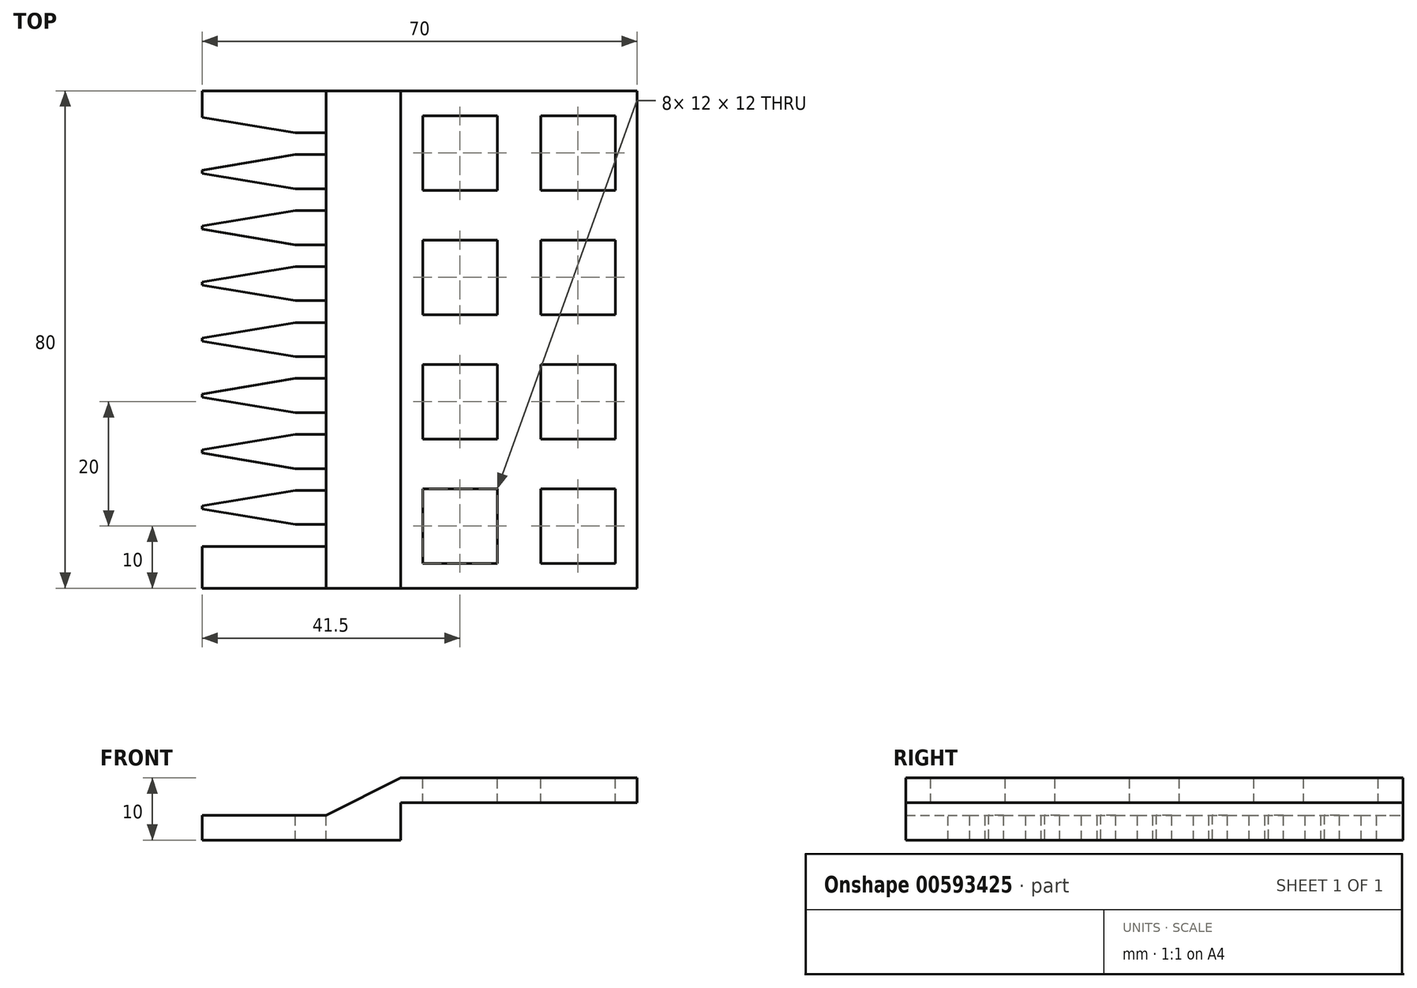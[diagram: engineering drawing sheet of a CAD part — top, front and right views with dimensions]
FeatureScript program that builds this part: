
annotation { "Feature Type Name" : "Feature", "Feature Type Description" : "" }
export const myFeature = defineFeature(function(context is Context, id is Id, definition is map)
    precondition{}
    {
        {
            var Q0;
            Q0=qCreatedBy(makeId("Front.planeOp"),FACE);
            var sketch = newSketch(context, id + "F0", { "sketchPlane" : qUnion([Q0])});
            skLineSegment(sketch, "E0", {"start": v(0, 0) * mm, "end": v(0, 4) * mm});
            skLineSegment(sketch, "E1", {"start": v(0, 4) * mm, "end": v(20, 4) * mm});
            skLineSegment(sketch, "E2", {"start": v(20, 4) * mm, "end": v(20, 10) * mm});
            skLineSegment(sketch, "E3", {"start": v(20, 10) * mm, "end": v(100, 10) * mm});
            skLineSegment(sketch, "E4", {"start": v(100, 10) * mm, "end": v(100, 6) * mm});
            skLineSegment(sketch, "E5", {"start": v(100, 6) * mm, "end": v(32, 6) * mm});
            skLineSegment(sketch, "E6", {"start": v(32, 6) * mm, "end": v(32, 0) * mm});
            skLineSegment(sketch, "E7", {"start": v(32, 0) * mm, "end": v(0, 0) * mm});
            skSolve(sketch);
        }
        {
            var Q0;
            Q0 = qSketchRegion(id + "F0", true);
            extrude(context, id + "F1", {"entities" : qUnion([Q0]), "depth" : 80 * mm, "offsetDistance" : 25 * mm});
        }
        {
            var Q0;
            Q0=makeQuery(id+"F1.opExtrude","SWEPT_FACE",FACE,{"disambiguationData":[OSD([sQuery(id+"F0.wireOp",EDGE,"E1")])]});
            var sketch = newSketch(context, id + "F2", { "sketchPlane" : qUnion([Q0])});
            skLineSegment(sketch, "E8", {"start": v(0, -40) * mm, "end": v(20, -40) * mm, "construction": true});
            skLineSegment(sketch, "E9.bottom", {"start": v(0, -37.25) * mm, "end": v(20, -37.25) * mm});
            skLineSegment(sketch, "E9.top", {"start": v(0, -33.75) * mm, "end": v(20, -33.75) * mm});
            skLineSegment(sketch, "E9.left", {"start": v(0, -37.25) * mm, "end": v(0, -33.75) * mm});
            skLineSegment(sketch, "E9.right", {"start": v(20, -37.25) * mm, "end": v(20, -33.75) * mm});
            skLineSegment(sketch, "E10.bottom", {"start": v(0, -28.25) * mm, "end": v(20, -28.25) * mm});
            skLineSegment(sketch, "E10.top", {"start": v(0, -24.75) * mm, "end": v(20, -24.75) * mm});
            skLineSegment(sketch, "E10.left", {"start": v(0, -28.25) * mm, "end": v(0, -24.75) * mm});
            skLineSegment(sketch, "E10.right", {"start": v(20, -28.25) * mm, "end": v(20, -24.75) * mm});
            skLineSegment(sketch, "E11.bottom", {"start": v(0, -19.25) * mm, "end": v(20, -19.25) * mm});
            skLineSegment(sketch, "E11.top", {"start": v(0, -15.75) * mm, "end": v(20, -15.75) * mm});
            skLineSegment(sketch, "E11.left", {"start": v(0, -19.25) * mm, "end": v(0, -15.75) * mm});
            skLineSegment(sketch, "E11.right", {"start": v(20, -19.25) * mm, "end": v(20, -15.75) * mm});
            skLineSegment(sketch, "E12.bottom", {"start": v(0, -10.25) * mm, "end": v(20, -10.25) * mm});
            skLineSegment(sketch, "E12.top", {"start": v(0, -6.75) * mm, "end": v(20, -6.75) * mm});
            skLineSegment(sketch, "E12.left", {"start": v(0, -10.25) * mm, "end": v(0, -6.75) * mm});
            skLineSegment(sketch, "E12.right", {"start": v(20, -10.25) * mm, "end": v(20, -6.75) * mm});
            skLineSegment(sketch, "E13", {"start": v(10, -10.25) * mm, "end": v(10, -15.75) * mm, "construction": true});
            skLineSegment(sketch, "E14", {"start": v(10, -24.75) * mm, "end": v(10, -19.25) * mm, "construction": true});
            skLineSegment(sketch, "E15", {"start": v(10, -28.25) * mm, "end": v(10, -33.75) * mm, "construction": true});
            skLineSegment(sketch, "E16.MirrorCS", {"start": v(20, -69.75) * mm, "end": v(20, -73.25) * mm});
            skLineSegment(sketch, "E17.MirrorCS", {"start": v(0, -55.25) * mm, "end": v(20, -55.25) * mm});
            skLineSegment(sketch, "E18.MirrorCS", {"start": v(0, -46.25) * mm, "end": v(20, -46.25) * mm});
            skLineSegment(sketch, "E19.MirrorCS", {"start": v(0, -60.75) * mm, "end": v(20, -60.75) * mm});
            skLineSegment(sketch, "E20.MirrorCS", {"start": v(10, -69.75) * mm, "end": v(10, -64.25) * mm, "construction": true});
            skLineSegment(sketch, "E21.MirrorCS", {"start": v(0, -42.75) * mm, "end": v(0, -46.25) * mm});
            skLineSegment(sketch, "E22.MirrorCS", {"start": v(0, -73.25) * mm, "end": v(20, -73.25) * mm});
            skLineSegment(sketch, "E23.MirrorCS", {"start": v(0, -51.75) * mm, "end": v(0, -55.25) * mm});
            skLineSegment(sketch, "E24.MirrorCS", {"start": v(0, -42.75) * mm, "end": v(20, -42.75) * mm});
            skLineSegment(sketch, "E25.MirrorCS", {"start": v(10, -55.25) * mm, "end": v(10, -60.75) * mm, "construction": true});
            skLineSegment(sketch, "E26.MirrorCS", {"start": v(0, -69.75) * mm, "end": v(0, -73.25) * mm});
            skLineSegment(sketch, "E27.MirrorCS", {"start": v(20, -51.75) * mm, "end": v(20, -55.25) * mm});
            skLineSegment(sketch, "E28.MirrorCS", {"start": v(20, -42.75) * mm, "end": v(20, -46.25) * mm});
            skLineSegment(sketch, "E29.MirrorCS", {"start": v(0, -60.75) * mm, "end": v(0, -64.25) * mm});
            skLineSegment(sketch, "E30.MirrorCS", {"start": v(0, -69.75) * mm, "end": v(20, -69.75) * mm});
            skLineSegment(sketch, "E31.MirrorCS", {"start": v(10, -51.75) * mm, "end": v(10, -46.25) * mm, "construction": true});
            skLineSegment(sketch, "E32.MirrorCS", {"start": v(20, -60.75) * mm, "end": v(20, -64.25) * mm});
            skLineSegment(sketch, "E33.MirrorCS", {"start": v(0, -51.75) * mm, "end": v(20, -51.75) * mm});
            skLineSegment(sketch, "E34.MirrorCS", {"start": v(0, -64.25) * mm, "end": v(20, -64.25) * mm});
            skSolve(sketch);
        }
        {
            var Q0;
            Q0 = qSketchRegion(id + "F2", true);
            extrude(context, id + "F3", {"entities" : qUnion([Q0]), "operationType" : NewBodyOperationType.REMOVE, "endBound" : BoundingType.THROUGH_ALL, "oppositeDirection" : true, "depth" : 25 * mm, "offsetDistance" : 25 * mm});
        }
        {
            var Q0;
            Q0=makeQuery(id+"F1.opExtrude","SWEPT_EDGE",EDGE,{"disambiguationData":[OSD([sQuery(id+"F0.wireOp",EDGE,"E2"),sQuery(id+"F0.wireOp",EDGE,"E3")])]});
            chamfer(context, id + "F4", {"entities" : qUnion([Q0]), "chamferType" : ChamferType.TWO_OFFSETS, "width1" : 6 * mm, "oppositeDirection" : false, "width2" : 12 * mm, "tangentPropagation" : true});
        }
        {
            var Q0;
            Q0=makeQuery(id+"F3.boolean.opBoolean","COPY",EDGE,{"derivedFrom":makeQuery(id+"F3.opExtrude","SWEPT_EDGE",EDGE,{"disambiguationData":[OSD([sQuery(id+"F0.wireOp",EDGE,"E0"),sQuery(id+"F0.wireOp",EDGE,"E1"),sQuery(id+"F2.wireOp",EDGE,"E12.top"),sQuery(id+"F2.wireOp",EDGE,"E12.left")])]})});
            var Q1;
            Q1=makeQuery(id+"F3.boolean.opBoolean","COPY",EDGE,{"derivedFrom":makeQuery(id+"F3.opExtrude","SWEPT_EDGE",EDGE,{"disambiguationData":[OSD([sQuery(id+"F0.wireOp",EDGE,"E0"),sQuery(id+"F0.wireOp",EDGE,"E1"),sQuery(id+"F2.wireOp",EDGE,"E11.top"),sQuery(id+"F2.wireOp",EDGE,"E11.left")])]})});
            var Q2;
            Q2=makeQuery(id+"F3.boolean.opBoolean","COPY",EDGE,{"derivedFrom":makeQuery(id+"F3.opExtrude","SWEPT_EDGE",EDGE,{"disambiguationData":[OSD([sQuery(id+"F0.wireOp",EDGE,"E0"),sQuery(id+"F0.wireOp",EDGE,"E1"),sQuery(id+"F2.wireOp",EDGE,"E10.top"),sQuery(id+"F2.wireOp",EDGE,"E10.left")])]})});
            var Q3;
            Q3=makeQuery(id+"F3.boolean.opBoolean","COPY",EDGE,{"derivedFrom":makeQuery(id+"F3.opExtrude","SWEPT_EDGE",EDGE,{"disambiguationData":[OSD([sQuery(id+"F0.wireOp",EDGE,"E0"),sQuery(id+"F0.wireOp",EDGE,"E1"),sQuery(id+"F2.wireOp",EDGE,"E9.top"),sQuery(id+"F2.wireOp",EDGE,"E9.left")])]})});
            var Q4;
            Q4=makeQuery(id+"F3.boolean.opBoolean","COPY",EDGE,{"derivedFrom":makeQuery(id+"F3.opExtrude","SWEPT_EDGE",EDGE,{"disambiguationData":[OSD([sQuery(id+"F0.wireOp",EDGE,"E0"),sQuery(id+"F0.wireOp",EDGE,"E1"),sQuery(id+"F2.wireOp",EDGE,"E21.MirrorCS"),sQuery(id+"F2.wireOp",EDGE,"E24.MirrorCS")])]})});
            var Q5;
            Q5=makeQuery(id+"F3.boolean.opBoolean","COPY",EDGE,{"derivedFrom":makeQuery(id+"F3.opExtrude","SWEPT_EDGE",EDGE,{"disambiguationData":[OSD([sQuery(id+"F0.wireOp",EDGE,"E0"),sQuery(id+"F0.wireOp",EDGE,"E1"),sQuery(id+"F2.wireOp",EDGE,"E23.MirrorCS"),sQuery(id+"F2.wireOp",EDGE,"E33.MirrorCS")])]})});
            var Q6;
            Q6=makeQuery(id+"F3.boolean.opBoolean","COPY",EDGE,{"derivedFrom":makeQuery(id+"F3.opExtrude","SWEPT_EDGE",EDGE,{"disambiguationData":[OSD([sQuery(id+"F0.wireOp",EDGE,"E0"),sQuery(id+"F0.wireOp",EDGE,"E1"),sQuery(id+"F2.wireOp",EDGE,"E19.MirrorCS"),sQuery(id+"F2.wireOp",EDGE,"E29.MirrorCS")])]})});
            var Q7;
            Q7=makeQuery(id+"F3.boolean.opBoolean","COPY",EDGE,{"derivedFrom":makeQuery(id+"F3.opExtrude","SWEPT_EDGE",EDGE,{"disambiguationData":[OSD([sQuery(id+"F0.wireOp",EDGE,"E0"),sQuery(id+"F0.wireOp",EDGE,"E1"),sQuery(id+"F2.wireOp",EDGE,"E26.MirrorCS"),sQuery(id+"F2.wireOp",EDGE,"E30.MirrorCS")])]})});
            chamfer(context, id + "F5", {"entities" : qUnion([Q0, Q1, Q2, Q3, Q4, Q5, Q6, Q7]), "chamferType" : ChamferType.TWO_OFFSETS, "width1" : 2.5 * mm, "oppositeDirection" : false, "width2" : 15 * mm, "tangentPropagation" : true});
        }
        {
            var Q0;
            Q0=makeQuery(id+"F3.boolean.opBoolean","COPY",EDGE,{"derivedFrom":makeQuery(id+"F3.opExtrude","SWEPT_EDGE",EDGE,{"disambiguationData":[OSD([sQuery(id+"F0.wireOp",EDGE,"E0"),sQuery(id+"F0.wireOp",EDGE,"E1"),sQuery(id+"F2.wireOp",EDGE,"E12.bottom"),sQuery(id+"F2.wireOp",EDGE,"E12.left")])]})});
            var Q1;
            Q1=makeQuery(id+"F3.boolean.opBoolean","COPY",EDGE,{"derivedFrom":makeQuery(id+"F3.opExtrude","SWEPT_EDGE",EDGE,{"disambiguationData":[OSD([sQuery(id+"F0.wireOp",EDGE,"E0"),sQuery(id+"F0.wireOp",EDGE,"E1"),sQuery(id+"F2.wireOp",EDGE,"E11.bottom"),sQuery(id+"F2.wireOp",EDGE,"E11.left")])]})});
            var Q2;
            Q2=makeQuery(id+"F3.boolean.opBoolean","COPY",EDGE,{"derivedFrom":makeQuery(id+"F3.opExtrude","SWEPT_EDGE",EDGE,{"disambiguationData":[OSD([sQuery(id+"F0.wireOp",EDGE,"E0"),sQuery(id+"F0.wireOp",EDGE,"E1"),sQuery(id+"F2.wireOp",EDGE,"E10.bottom"),sQuery(id+"F2.wireOp",EDGE,"E10.left")])]})});
            var Q3;
            Q3=makeQuery(id+"F3.boolean.opBoolean","COPY",EDGE,{"derivedFrom":makeQuery(id+"F3.opExtrude","SWEPT_EDGE",EDGE,{"disambiguationData":[OSD([sQuery(id+"F0.wireOp",EDGE,"E0"),sQuery(id+"F0.wireOp",EDGE,"E1"),sQuery(id+"F2.wireOp",EDGE,"E9.bottom"),sQuery(id+"F2.wireOp",EDGE,"E9.left")])]})});
            var Q4;
            Q4=makeQuery(id+"F3.boolean.opBoolean","COPY",EDGE,{"derivedFrom":makeQuery(id+"F3.opExtrude","SWEPT_EDGE",EDGE,{"disambiguationData":[OSD([sQuery(id+"F0.wireOp",EDGE,"E0"),sQuery(id+"F0.wireOp",EDGE,"E1"),sQuery(id+"F2.wireOp",EDGE,"E18.MirrorCS"),sQuery(id+"F2.wireOp",EDGE,"E21.MirrorCS")])]})});
            var Q5;
            Q5=makeQuery(id+"F3.boolean.opBoolean","COPY",EDGE,{"derivedFrom":makeQuery(id+"F3.opExtrude","SWEPT_EDGE",EDGE,{"disambiguationData":[OSD([sQuery(id+"F0.wireOp",EDGE,"E0"),sQuery(id+"F0.wireOp",EDGE,"E1"),sQuery(id+"F2.wireOp",EDGE,"E17.MirrorCS"),sQuery(id+"F2.wireOp",EDGE,"E23.MirrorCS")])]})});
            var Q6;
            Q6=makeQuery(id+"F3.boolean.opBoolean","COPY",EDGE,{"derivedFrom":makeQuery(id+"F3.opExtrude","SWEPT_EDGE",EDGE,{"disambiguationData":[OSD([sQuery(id+"F0.wireOp",EDGE,"E0"),sQuery(id+"F0.wireOp",EDGE,"E1"),sQuery(id+"F2.wireOp",EDGE,"E29.MirrorCS"),sQuery(id+"F2.wireOp",EDGE,"E34.MirrorCS")])]})});
            var Q7;
            Q7=makeQuery(id+"F3.boolean.opBoolean","COPY",EDGE,{"derivedFrom":makeQuery(id+"F3.opExtrude","SWEPT_EDGE",EDGE,{"disambiguationData":[OSD([sQuery(id+"F0.wireOp",EDGE,"E0"),sQuery(id+"F0.wireOp",EDGE,"E1"),sQuery(id+"F2.wireOp",EDGE,"E22.MirrorCS"),sQuery(id+"F2.wireOp",EDGE,"E26.MirrorCS")])]})});
            chamfer(context, id + "F6", {"entities" : qUnion([Q0, Q1, Q2, Q3, Q4, Q5, Q6, Q7]), "chamferType" : ChamferType.TWO_OFFSETS, "width1" : 15 * mm, "oppositeDirection" : false, "width2" : 2.5 * mm, "tangentPropagation" : true});
        }
        {
            var Q0;
            Q0=makeQuery(id+"F1.opExtrude","SWEPT_FACE",FACE,{"disambiguationData":[OSD([sQuery(id+"F0.wireOp",EDGE,"E3")])]});
            var sketch = newSketch(context, id + "F7", { "sketchPlane" : qUnion([Q0])});
            skLineSegment(sketch, "E35.bottom", {"start": v(100, 0) * mm, "end": v(70, 0) * mm});
            skLineSegment(sketch, "E35.top", {"start": v(100, -80) * mm, "end": v(70, -80) * mm});
            skLineSegment(sketch, "E35.left", {"start": v(100, 0) * mm, "end": v(100, -80) * mm});
            skLineSegment(sketch, "E35.right", {"start": v(70, 0) * mm, "end": v(70, -80) * mm});
            skSolve(sketch);
        }
        {
            var Q0;
            Q0 = qSketchRegion(id + "F7", true);
            extrude(context, id + "F8", {"entities" : qUnion([Q0]), "operationType" : NewBodyOperationType.REMOVE, "oppositeDirection" : true, "depth" : 25 * mm, "offsetDistance" : 25 * mm});
        }
        {
            var Q0;
            Q0=makeQuery(id+"F1.opExtrude","SWEPT_FACE",FACE,{"disambiguationData":[OSD([sQuery(id+"F0.wireOp",EDGE,"E3")])]});
            var sketch = newSketch(context, id + "F9", { "sketchPlane" : qUnion([Q0])});
            skLineSegment(sketch, "E36.bottom", {"start": v(35.5, -4) * mm, "end": v(47.5, -4) * mm});
            skLineSegment(sketch, "E36.top", {"start": v(35.5, -16) * mm, "end": v(47.5, -16) * mm});
            skLineSegment(sketch, "E36.left", {"start": v(35.5, -4) * mm, "end": v(35.5, -16) * mm});
            skLineSegment(sketch, "E36.right", {"start": v(47.5, -4) * mm, "end": v(47.5, -16) * mm});
            skLineSegment(sketch, "E37", {"start": v(51, 0) * mm, "end": v(51, -80) * mm, "construction": true});
            skLineSegment(sketch, "E38", {"start": v(41.5, -4) * mm, "end": v(41.5, -16) * mm, "construction": true});
            skLineSegment(sketch, "E39", {"start": v(35.5, -10) * mm, "end": v(47.5, -10) * mm, "construction": true});
            skLineSegment(sketch, "E40", {"start": v(70, -40) * mm, "end": v(32, -40) * mm, "construction": true});
            skLineSegment(sketch, "E41.0.1.0", {"start": v(35.5, -30) * mm, "end": v(47.5, -30) * mm, "construction": true});
            skLineSegment(sketch, "E41.0.1.1", {"start": v(47.5, -24) * mm, "end": v(47.5, -36) * mm});
            skLineSegment(sketch, "E41.0.1.2", {"start": v(41.5, -24) * mm, "end": v(41.5, -36) * mm, "construction": true});
            skLineSegment(sketch, "E41.0.1.3", {"start": v(35.5, -24) * mm, "end": v(47.5, -24) * mm});
            skLineSegment(sketch, "E41.0.1.4", {"start": v(35.5, -36) * mm, "end": v(47.5, -36) * mm});
            skLineSegment(sketch, "E41.0.1.5", {"start": v(35.5, -24) * mm, "end": v(35.5, -36) * mm});
            skLineSegment(sketch, "E41.0.2.0", {"start": v(35.5, -50) * mm, "end": v(47.5, -50) * mm, "construction": true});
            skLineSegment(sketch, "E41.0.2.1", {"start": v(47.5, -44) * mm, "end": v(47.5, -56) * mm});
            skLineSegment(sketch, "E41.0.2.2", {"start": v(41.5, -44) * mm, "end": v(41.5, -56) * mm, "construction": true});
            skLineSegment(sketch, "E41.0.2.3", {"start": v(35.5, -44) * mm, "end": v(47.5, -44) * mm});
            skLineSegment(sketch, "E41.0.2.4", {"start": v(35.5, -56) * mm, "end": v(47.5, -56) * mm});
            skLineSegment(sketch, "E41.0.2.5", {"start": v(35.5, -44) * mm, "end": v(35.5, -56) * mm});
            skLineSegment(sketch, "E41.0.3.0", {"start": v(35.5, -70) * mm, "end": v(47.5, -70) * mm, "construction": true});
            skLineSegment(sketch, "E41.0.3.1", {"start": v(47.5, -64) * mm, "end": v(47.5, -76) * mm});
            skLineSegment(sketch, "E41.0.3.2", {"start": v(41.5, -64) * mm, "end": v(41.5, -76) * mm, "construction": true});
            skLineSegment(sketch, "E41.0.3.3", {"start": v(35.5, -64) * mm, "end": v(47.5, -64) * mm});
            skLineSegment(sketch, "E41.0.3.4", {"start": v(35.5, -76) * mm, "end": v(47.5, -76) * mm});
            skLineSegment(sketch, "E41.0.3.5", {"start": v(35.5, -64) * mm, "end": v(35.5, -76) * mm});
            skLineSegment(sketch, "E41.direction1", {"start": v(35.5, -16) * mm, "end": v(60.5, -16) * mm, "construction": true});
            skLineSegment(sketch, "E41.direction2", {"start": v(35.5, -16) * mm, "end": v(35.5, -36) * mm, "construction": true});
            skLineSegment(sketch, "E42.MirrorCS", {"start": v(66.5, -24) * mm, "end": v(66.5, -36) * mm});
            skLineSegment(sketch, "E43.MirrorCS", {"start": v(54.5, -64) * mm, "end": v(54.5, -76) * mm});
            skLineSegment(sketch, "E44.MirrorCS", {"start": v(66.5, -4) * mm, "end": v(54.5, -4) * mm});
            skLineSegment(sketch, "E45.MirrorCS", {"start": v(66.5, -16) * mm, "end": v(54.5, -16) * mm});
            skLineSegment(sketch, "E46.MirrorCS", {"start": v(66.5, -44) * mm, "end": v(66.5, -56) * mm});
            skLineSegment(sketch, "E47.MirrorCS", {"start": v(66.5, -4) * mm, "end": v(66.5, -16) * mm});
            skLineSegment(sketch, "E48.MirrorCS", {"start": v(66.5, -56) * mm, "end": v(54.5, -56) * mm});
            skLineSegment(sketch, "E49.MirrorCS", {"start": v(54.5, -44) * mm, "end": v(54.5, -56) * mm});
            skLineSegment(sketch, "E50.MirrorCS", {"start": v(66.5, -50) * mm, "end": v(54.5, -50) * mm, "construction": true});
            skLineSegment(sketch, "E51.MirrorCS", {"start": v(66.5, -76) * mm, "end": v(54.5, -76) * mm});
            skLineSegment(sketch, "E52.MirrorCS", {"start": v(54.5, -4) * mm, "end": v(54.5, -16) * mm});
            skLineSegment(sketch, "E53.MirrorCS", {"start": v(60.5, -44) * mm, "end": v(60.5, -56) * mm, "construction": true});
            skLineSegment(sketch, "E54.MirrorCS", {"start": v(60.5, -4) * mm, "end": v(60.5, -16) * mm, "construction": true});
            skLineSegment(sketch, "E55.MirrorCS", {"start": v(66.5, -10) * mm, "end": v(54.5, -10) * mm, "construction": true});
            skLineSegment(sketch, "E56.MirrorCS", {"start": v(66.5, -16) * mm, "end": v(66.5, -36) * mm, "construction": true});
            skLineSegment(sketch, "E57.MirrorCS", {"start": v(66.5, -64) * mm, "end": v(66.5, -76) * mm});
            skLineSegment(sketch, "E58.MirrorCS", {"start": v(66.5, -30) * mm, "end": v(54.5, -30) * mm, "construction": true});
            skLineSegment(sketch, "E59.MirrorCS", {"start": v(54.5, -24) * mm, "end": v(54.5, -36) * mm});
            skLineSegment(sketch, "E60.MirrorCS", {"start": v(60.5, -24) * mm, "end": v(60.5, -36) * mm, "construction": true});
            skLineSegment(sketch, "E61.MirrorCS", {"start": v(66.5, -24) * mm, "end": v(54.5, -24) * mm});
            skLineSegment(sketch, "E62.MirrorCS", {"start": v(66.5, -36) * mm, "end": v(54.5, -36) * mm});
            skLineSegment(sketch, "E63.MirrorCS", {"start": v(60.5, -64) * mm, "end": v(60.5, -76) * mm, "construction": true});
            skLineSegment(sketch, "E64.MirrorCS", {"start": v(66.5, -70) * mm, "end": v(54.5, -70) * mm, "construction": true});
            skLineSegment(sketch, "E65.MirrorCS", {"start": v(66.5, -44) * mm, "end": v(54.5, -44) * mm});
            skLineSegment(sketch, "E66.MirrorCS", {"start": v(66.5, -64) * mm, "end": v(54.5, -64) * mm});
            skSolve(sketch);
        }
        {
            var Q0;
            Q0 = qSketchRegion(id + "F9", true);
            extrude(context, id + "F10", {"entities" : qUnion([Q0]), "operationType" : NewBodyOperationType.REMOVE, "endBound" : BoundingType.THROUGH_ALL, "oppositeDirection" : true, "depth" : 25 * mm, "offsetDistance" : 25 * mm});
        }
    });
